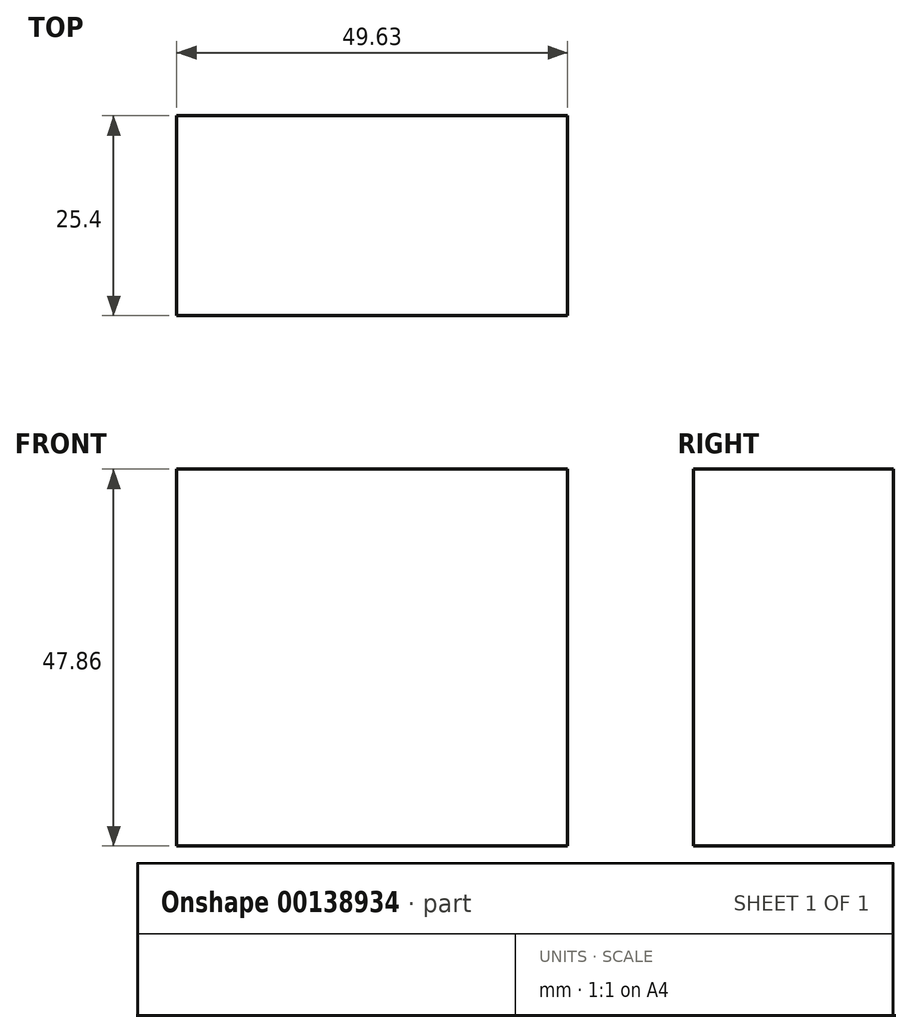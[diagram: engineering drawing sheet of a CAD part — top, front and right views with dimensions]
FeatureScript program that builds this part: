
annotation { "Feature Type Name" : "Feature", "Feature Type Description" : "" }
export const myFeature = defineFeature(function(context is Context, id is Id, definition is map)
    precondition{}
    {
        {
            var Q0;
            Q0=qCreatedBy(makeId("Front.planeOp"),FACE);
            var sketch = newSketch(context, id + "F0", { "sketchPlane" : qUnion([Q0])});
            skLineSegment(sketch, "E0.bottom", {"start": v(-60.27, 61.48) * mm, "end": v(-10.64, 61.48) * mm});
            skLineSegment(sketch, "E0.top", {"start": v(-60.27, 13.62) * mm, "end": v(-10.64, 13.62) * mm});
            skLineSegment(sketch, "E0.left", {"start": v(-60.27, 61.48) * mm, "end": v(-60.27, 13.62) * mm});
            skLineSegment(sketch, "E0.right", {"start": v(-10.64, 61.48) * mm, "end": v(-10.64, 13.62) * mm});
            skSolve(sketch);
        }
        {
            var Q0;
            Q0=makeQuery(id+"F0.imprint","IMPRINT",FACE,{"disambiguationData":[TD([[makeQuery(id+"F0.imprint","IMPRINT",EDGE,{"derivedFrom":sQuery(id+"F0.wireOp",EDGE,"E0.bottom")}),-1.0]])]});
            extrude(context, id + "F1", {"entities" : qUnion([Q0]), "depth" : 25.4 * mm});
        }
        {
            var Q0;
            Q0=makeQuery(id+"F1.opExtrude","CAP_FACE",FACE,{"disambiguationData":[OSD([sQuery(id+"F0.wireOp",EDGE,"E0.bottom"),sQuery(id+"F0.wireOp",EDGE,"E0.top"),sQuery(id+"F0.wireOp",EDGE,"E0.left"),sQuery(id+"F0.wireOp",EDGE,"E0.right")])],"isStart":false});
            var sketch = newSketch(context, id + "F2", { "sketchPlane" : qUnion([Q0])});
            skLineSegment(sketch, "E1.bottom", {"start": v(-52.7, 51.65) * mm, "end": v(-25.62, 51.65) * mm});
            skLineSegment(sketch, "E1.top", {"start": v(-52.7, 29.57) * mm, "end": v(-25.62, 29.57) * mm});
            skLineSegment(sketch, "E1.left", {"start": v(-52.7, 51.65) * mm, "end": v(-52.7, 29.57) * mm});
            skLineSegment(sketch, "E1.right", {"start": v(-25.62, 51.65) * mm, "end": v(-25.62, 29.57) * mm});
            skSolve(sketch);
        }
        {
            var Q0;
            Q0=makeQuery(id+"F2.imprint","IMPRINT",FACE,{"disambiguationData":[TD([[makeQuery(id+"F2.imprint","IMPRINT",EDGE,{"derivedFrom":sQuery(id+"F2.wireOp",EDGE,"E1.bottom")}),-1.0]])]});
            extrude(context, id + "F3", {"entities" : qUnion([Q0]), "operationType" : NewBodyOperationType.ADD, "oppositeDirection" : true, "depth" : 25.4 * mm});
        }
        {
            var Q0;
            Q0=makeQuery(id+"F1.opExtrude","CAP_FACE",FACE,{"disambiguationData":[OSD([sQuery(id+"F0.wireOp",EDGE,"E0.bottom"),sQuery(id+"F0.wireOp",EDGE,"E0.top"),sQuery(id+"F0.wireOp",EDGE,"E0.left"),sQuery(id+"F0.wireOp",EDGE,"E0.right")])],"isStart":true});
            extrude(context, id + "F4", {"entities" : qUnion([Q0]), "operationType" : NewBodyOperationType.REMOVE, "depth" : 25.4 * mm});
        }
    });
